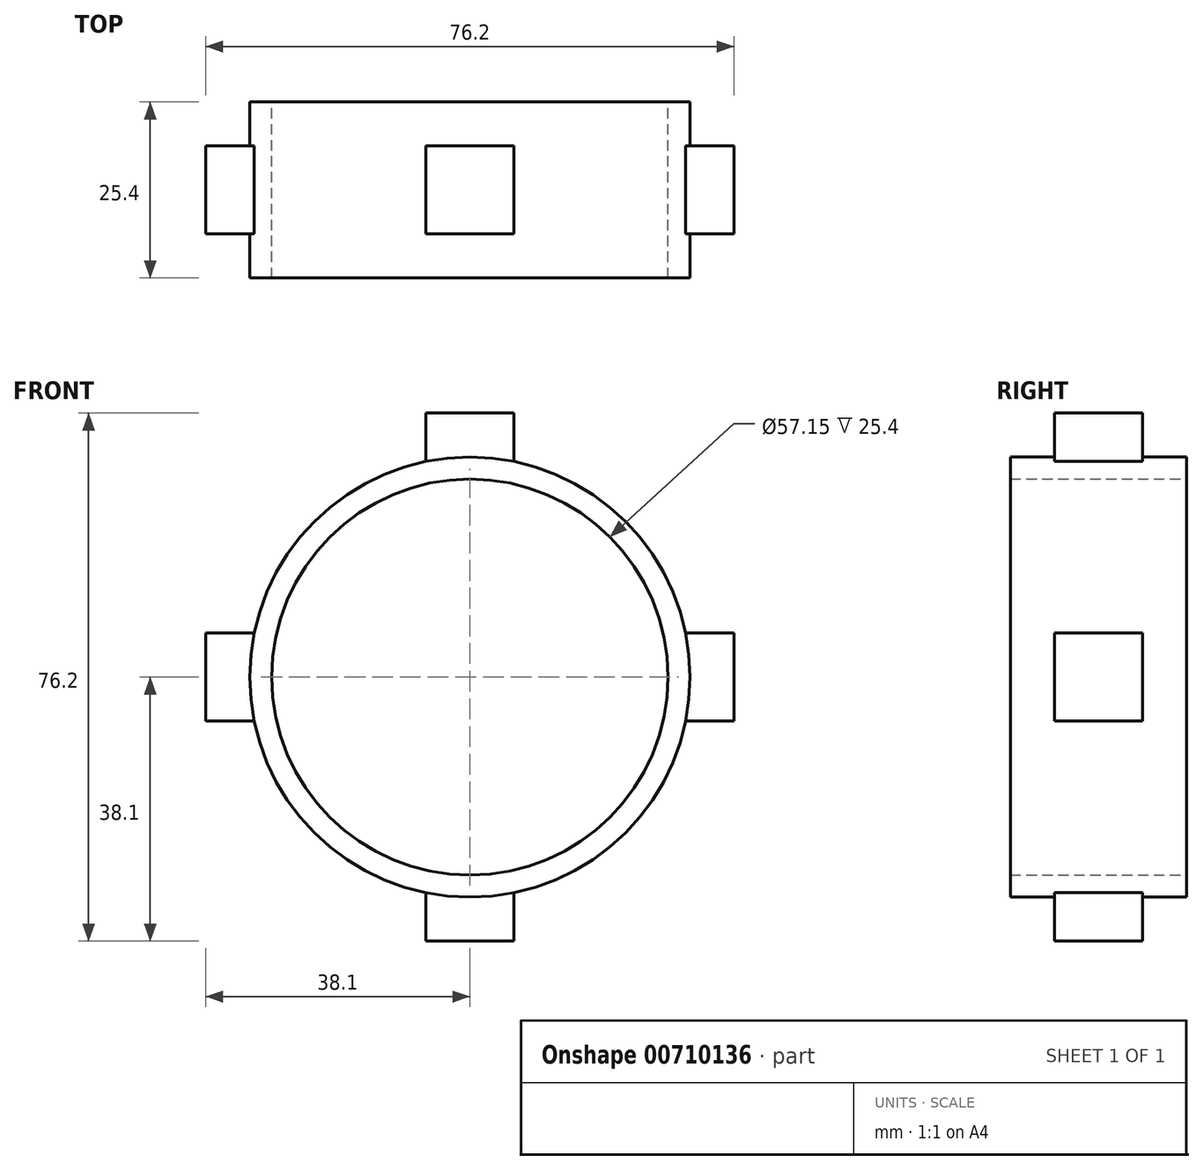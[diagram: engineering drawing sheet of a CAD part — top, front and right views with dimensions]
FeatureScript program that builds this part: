
annotation { "Feature Type Name" : "Feature", "Feature Type Description" : "" }
export const myFeature = defineFeature(function(context is Context, id is Id, definition is map)
    precondition{}
    {
        {
            var Q0;
            Q0=qCreatedBy(makeId("Front.planeOp"),FACE);
            var sketch = newSketch(context, id + "F0", { "sketchPlane" : qUnion([Q0])});
            skCircle(sketch, "E0", {"center": v(0, 0) * mm, "radius": 31.75 * mm});
            skCircle(sketch, "E1", {"center": v(0, 0) * mm, "radius": 28.58 * mm});
            skSolve(sketch);
        }
        {
            var Q0;
            Q0=makeQuery(id+"F0.imprint","IMPRINT",FACE,{"disambiguationData":[TD([[makeQuery(id+"F0.imprint","IMPRINT",EDGE,{"derivedFrom":sQuery(id+"F0.wireOp",EDGE,"E0")}),1.0]])]});
            extrude(context, id + "F1", {"entities" : qUnion([Q0]), "depth" : 25.4 * mm, "offsetDistance" : 25.4 * mm});
        }
        {
            var Q0;
            Q0=qCreatedBy(makeId("Front.planeOp"),FACE);
            cPlane(context, id + "F2", {"entities" : qUnion([Q0]), "cplaneType" : CPlaneType.OFFSET, "offset" : 6.35 * mm, "width" : 152.4 * mm, "height" : 152.4 * mm});
        }
        {
            var Q0;
            Q0=qCreatedBy(id+"F2.planeOp",FACE);
            var sketch = newSketch(context, id + "F3", { "sketchPlane" : qUnion([Q0])});
            skLineSegment(sketch, "E2.bottom", {"start": v(6.35, 30.48) * mm, "end": v(-6.35, 30.48) * mm});
            skLineSegment(sketch, "E2.top", {"start": v(6.35, 38.1) * mm, "end": v(-6.35, 38.1) * mm});
            skLineSegment(sketch, "E2.left", {"start": v(6.35, 30.48) * mm, "end": v(6.35, 38.1) * mm});
            skLineSegment(sketch, "E2.right", {"start": v(-6.35, 30.48) * mm, "end": v(-6.35, 38.1) * mm});
            skLineSegment(sketch, "E3.1.0", {"start": v(-30.48, -6.35) * mm, "end": v(-38.1, -6.35) * mm});
            skLineSegment(sketch, "E3.1.1", {"start": v(-30.48, 6.35) * mm, "end": v(-38.1, 6.35) * mm});
            skLineSegment(sketch, "E3.1.2", {"start": v(-38.1, 6.35) * mm, "end": v(-38.1, -6.35) * mm});
            skLineSegment(sketch, "E3.1.3", {"start": v(-30.48, 6.35) * mm, "end": v(-30.48, -6.35) * mm});
            skLineSegment(sketch, "E3.2.0", {"start": v(6.35, -30.48) * mm, "end": v(6.35, -38.1) * mm});
            skLineSegment(sketch, "E3.2.1", {"start": v(-6.35, -30.48) * mm, "end": v(-6.35, -38.1) * mm});
            skLineSegment(sketch, "E3.2.2", {"start": v(-6.35, -38.1) * mm, "end": v(6.35, -38.1) * mm});
            skLineSegment(sketch, "E3.2.3", {"start": v(-6.35, -30.48) * mm, "end": v(6.35, -30.48) * mm});
            skLineSegment(sketch, "E3.3.0", {"start": v(30.48, 6.35) * mm, "end": v(38.1, 6.35) * mm});
            skLineSegment(sketch, "E3.3.1", {"start": v(30.48, -6.35) * mm, "end": v(38.1, -6.35) * mm});
            skLineSegment(sketch, "E3.3.2", {"start": v(38.1, -6.35) * mm, "end": v(38.1, 6.35) * mm});
            skLineSegment(sketch, "E3.3.3", {"start": v(30.48, -6.35) * mm, "end": v(30.48, 6.35) * mm});
            skPoint(sketch, "E3.center", {"position": v(0, 0) * mm});
            skSolve(sketch);
        }
        {
            var Q0;
            Q0=makeQuery(id+"F3.imprint","IMPRINT",FACE,{"disambiguationData":[TD([[makeQuery(id+"F3.imprint","IMPRINT",EDGE,{"derivedFrom":sQuery(id+"F3.wireOp",EDGE,"E2.bottom")}),-1.0]])]});
            var Q1;
            Q1=makeQuery(id+"F3.imprint","IMPRINT",FACE,{"disambiguationData":[TD([[makeQuery(id+"F3.imprint","IMPRINT",EDGE,{"derivedFrom":sQuery(id+"F3.wireOp",EDGE,"E3.3.0")}),-1.0]])]});
            var Q2;
            Q2=makeQuery(id+"F3.imprint","IMPRINT",FACE,{"disambiguationData":[TD([[makeQuery(id+"F3.imprint","IMPRINT",EDGE,{"derivedFrom":sQuery(id+"F3.wireOp",EDGE,"E3.1.0")}),-1.0]])]});
            var Q3;
            Q3=makeQuery(id+"F3.imprint","IMPRINT",FACE,{"disambiguationData":[TD([[makeQuery(id+"F3.imprint","IMPRINT",EDGE,{"derivedFrom":sQuery(id+"F3.wireOp",EDGE,"E3.2.0")}),-1.0]])]});
            extrude(context, id + "F4", {"entities" : qUnion([Q0, Q1, Q2, Q3]), "operationType" : NewBodyOperationType.ADD, "depth" : 12.7 * mm, "offsetDistance" : 25.4 * mm});
        }
    });
